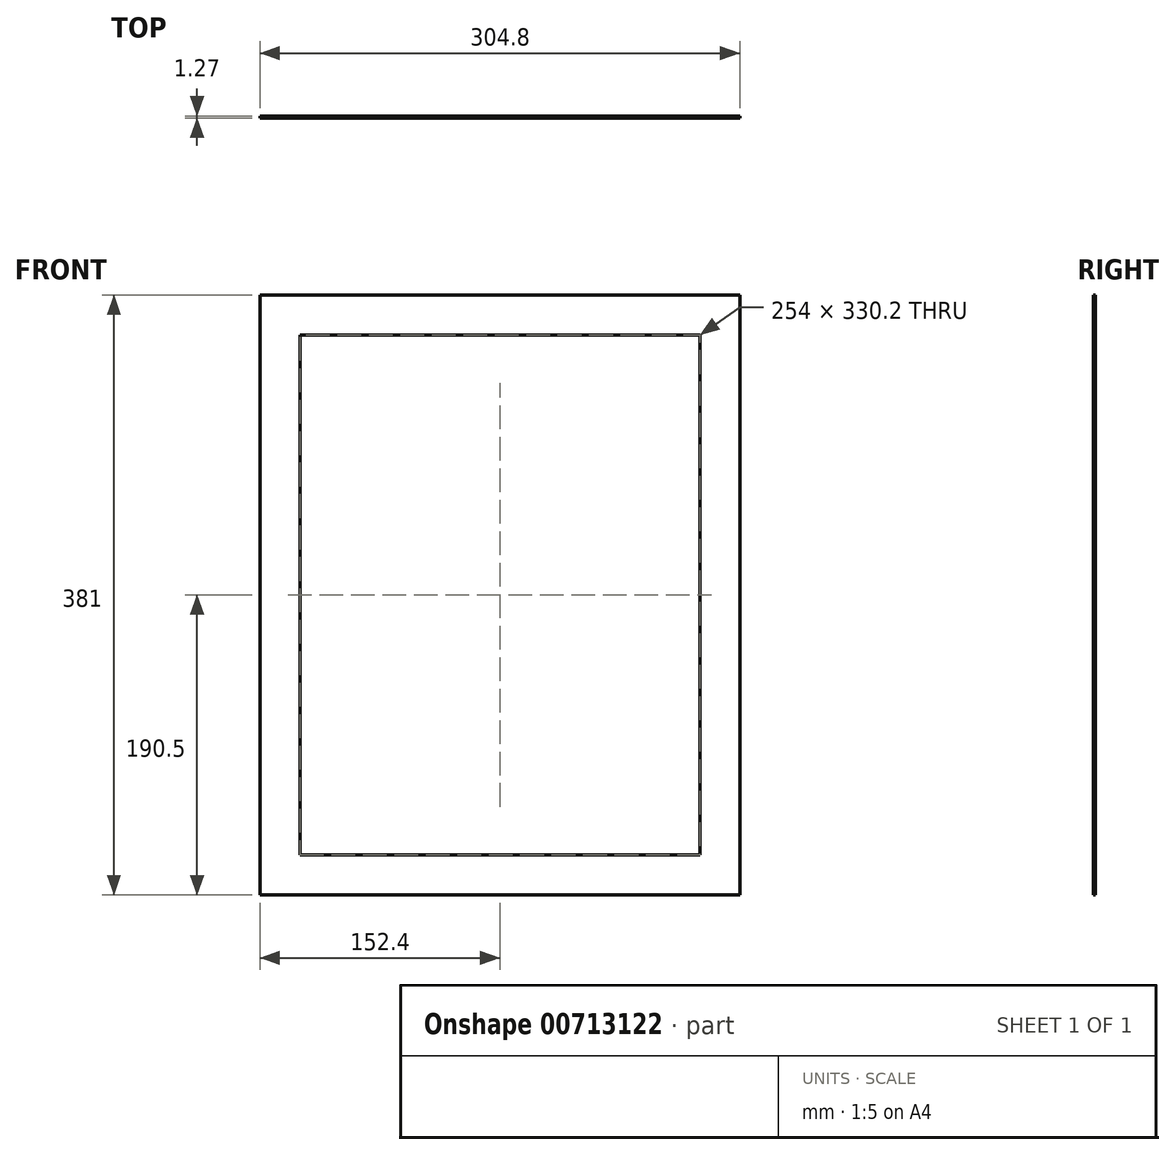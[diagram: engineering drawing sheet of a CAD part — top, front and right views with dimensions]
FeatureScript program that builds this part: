
annotation { "Feature Type Name" : "Feature", "Feature Type Description" : "" }
export const myFeature = defineFeature(function(context is Context, id is Id, definition is map)
    precondition{}
    {
        {
            var Q0;
            Q0=qCreatedBy(makeId("Front.planeOp"),FACE);
            var sketch = newSketch(context, id + "F0", { "sketchPlane" : qUnion([Q0])});
            skLineSegment(sketch, "E0.bottom", {"start": v(-152.4, 190.5) * mm, "end": v(152.4, 190.5) * mm});
            skLineSegment(sketch, "E0.top", {"start": v(-152.4, -190.5) * mm, "end": v(152.4, -190.5) * mm});
            skLineSegment(sketch, "E0.left", {"start": v(-152.4, 190.5) * mm, "end": v(-152.4, -190.5) * mm});
            skLineSegment(sketch, "E0.right", {"start": v(152.4, 190.5) * mm, "end": v(152.4, -190.5) * mm});
            skPoint(sketch, "E0.middle", {"position": v(0, 0) * mm});
            skLineSegment(sketch, "E1.0", {"start": v(-127, 165.1) * mm, "end": v(127, 165.1) * mm});
            skLineSegment(sketch, "E1.1", {"start": v(-127, 165.1) * mm, "end": v(-127, -165.1) * mm});
            skLineSegment(sketch, "E1.2", {"start": v(-127, -165.1) * mm, "end": v(127, -165.1) * mm});
            skLineSegment(sketch, "E1.3", {"start": v(127, 165.1) * mm, "end": v(127, -165.1) * mm});
            skSolve(sketch);
        }
        {
            var Q0;
            Q0=makeQuery(id+"F0.imprint","IMPRINT",FACE,{"disambiguationData":[TD([[makeQuery(id+"F0.imprint","IMPRINT",EDGE,{"derivedFrom":sQuery(id+"F0.wireOp",EDGE,"E0.bottom")}),-1.0]])]});
            extrude(context, id + "F1", {"entities" : qUnion([Q0]), "depth" : 1.27 * mm, "offsetDistance" : 25.4 * mm});
        }
    });
